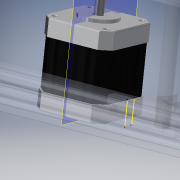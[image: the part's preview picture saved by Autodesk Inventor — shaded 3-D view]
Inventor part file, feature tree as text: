
AUTODESK INVENTOR PART (.ipt)
format: ipt  version: 2018 (Build 220112000, 112)  size: 1,120,256 bytes
history: native  units: mm
features: extrude x12, sketch x4, hole x4, fillet x4, plane x2, chamfer x2, pattern_linear x1, projected_geometry x1
ambient origin geometry x8: Origin, YZ Plane, XZ Plane, XY Plane, X Axis, Y Axis, Z Axis, Center Point
bodies: Solid1 (feature_tree)
feature tree (30):
  sketch  "Sketch1"  dims[d0=7.0mm d1=22.0mm]
  extrude  "Extrusion1"  Depth=22.0mm
  extrude  "Extrusion2"  Depth=31.0mm
  extrude  "Extrusion3"  Depth=3.0mm
  plane  "Work Plane2"
  extrude  "Extrusion7"  Depth=10.0mm
  extrude  "Extrusion8"  Depth=10.0mm
  chamfer  "Chamfer1"  Distance=42.0mm
  pattern_linear  "Rectangular Pattern2"  Spacing1=42.0mm  [1 undecoded]
  hole  "Hole1"  [1 undecoded]
  hole  "Hole2"  [1 undecoded]
  hole  "Hole3"  [1 undecoded]
  hole  "Hole4"  [1 undecoded]
  extrude  "Extrusion9"  Depth=10.0mm
  fillet  "Fillet1"  Radius=24.0mm
  fillet  "Fillet2"  Radius=2.0mm
  chamfer  "Chamfer2"  Distance=48.0mm
  fillet  "Fillet3"  [1 undecoded]
  sketch  "Sketch6"  dims[d10=3.0mm d11=3.0mm d12=3.0mm d39=42.0mm d40=42.0mm d41=135.0deg d42=51.618795mm d43=51.618795mm d44=25.809398mm d45=25.809398mm d46=24.0mm d47=0.0mm d48=2.0mm d49=0.0mm d50=48.0mm d51=0.0mm d60=-10.0mm d126=28.0mm d127=0.0mm d128=1.0mm d129=1.0mm d130=1.0mm d131=1.0mm d132=0.5mm d134=0.5mm d135=0.5mm d136=0.5mm d137=0.5mm d138=1.0mm d139=1.0mm d140=0.5mm d141=0.0mm d145=0.125mm d146=2.0mm d147=45.0deg d148=560.0mm d150=0.5mm d151=10.0mm d152=10.0mm d153=6.0mm d154=6.0mm d155=4.0mm d156=2.0mm d157=90.0deg d158=3.0mm d159=0.0mm d160=10.0mm d161=10.0mm d162=6.0mm d163=6.0mm d164=4.0mm d165=2.0mm d166=90.0deg d167=3.0mm d168=0.0mm d169=10.0mm d170=10.0mm d171=6.0mm d172=6.0mm d173=4.0mm d174=2.0mm d175=90.0deg d176=3.0mm d177=0.0mm d178=10.0mm d179=10.0mm d180=6.0mm d181=6.0mm d182=4.0mm d183=2.0mm d184=90.0deg d185=3.0mm d186=0.0mm d187=48.0mm d188=0.0mm d189=47.0mm d190=0.0mm d191=1.0mm d192=1.0mm d193=0.5mm d194=2.0mm d195=45.0deg d196=0.5mm d197=1.2mm d198=40.0mm d200=1.2mm d201=10.0mm d203=10.0mm d205=2.5mm d206=2.5mm d207=1.0mm d208=0.0mm d209=0.3mm d210=10.0mm d211=0.0mm d212=10.0mm d213=0.0mm d214=10.0mm d215=0.0mm d216=10.0mm d217=0.0mm d218=0.2mm d219=5.0mm d220=0.0mm d221=0.0mm]
  extrude  "Extrusion10"  Depth=10.0mm TaperAngle=0.0deg
  fillet  "Fillet4"  Radius=1.0mm
  extrude  "Extrusion11"  Depth=10.0mm
  extrude  "Extrusion12"  Depth=10.0mm
  extrude  "Extrusion13"  Depth=10.0mm
  extrude  "Extrusion14"  Depth=10.0mm
  extrude  "Extrusion15"  Depth=10.0mm
  plane  "Work Plane3"
  sketch  "Sketch4"  dims[d4=5.0mm d5=31.0mm]
  projected_geometry  "Projected Loop2"
  sketch  "Sketch5"  dims[d6=31.0mm d9=3.0mm]
note: 6 required parameter values undecoded (feature->parameter linkage not recoverable at this tier; creation-order binding heuristic only, values carry confidence <= 0.55)
